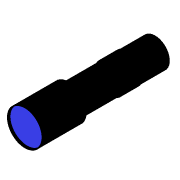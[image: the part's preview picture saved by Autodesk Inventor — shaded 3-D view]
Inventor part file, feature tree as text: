
AUTODESK INVENTOR PART (.ipt)
format: ipt  version: 2019 (Build 230136000, 136)  size: 128,512 bytes
history: native  units: mm
features: sketch x3, chamfer x2, extrude x2, other x1, revolve x1
ambient origin geometry x8: Origin, YZ Plane, XZ Plane, XY Plane, X Axis, Y Axis, Z Axis, Center Point
bodies: Body1 (feature_tree), Body2 (feature_tree)
feature tree (9):
  chamfer  "Chamfer1"  Distance=61.0mm
  chamfer  "Chamfer2"  Distance=74.5mm
  extrude  "Extrusion2"  Depth=4.9mm
  extrude  "Extrusion3"  Depth=4.9mm
  sketch  "Sketch1"  dims[d0=72.0mm]
  other  "Srf1"
  sketch  "Sketch3"  dims[d1=91.0mm]
  sketch  "Sketch4"  dims[d2=58.0mm d3=61.0mm d4=74.5mm d5=39.0mm d7=59.0mm d8=54.0mm d9=90.0deg d10=7.0mm d11=2.0mm d12=45.0deg d13=1.0mm d14=2.0mm d15=45.0deg d18=5.0mm d19=0.0mm d20=4.9mm d21=0.0mm]
  revolve  "RevolutionSrf1"  [1 undecoded]
note: 1 required parameter value undecoded (feature->parameter linkage not recoverable at this tier; creation-order binding heuristic only, values carry confidence <= 0.55)
